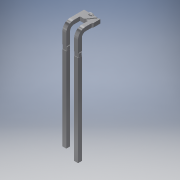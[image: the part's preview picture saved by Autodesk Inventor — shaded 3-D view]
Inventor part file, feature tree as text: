
AUTODESK INVENTOR PART (.ipt)
format: ipt  version: 2019.4 (Build 234330000, 330)  size: 351,744 bytes
history: native  units: mm
features: sketch x8, fillet x4, other x3, revolve x3, extrude x2, projected_geometry x2, sweep x1
ambient origin geometry x8: Origin, YZ Plane, XZ Plane, XY Plane, X Axis, Y Axis, Z Axis, Center Point
bodies: Body1 (feature_tree), Body2 (feature_tree)
feature tree (23):
  other  "Sólido1"
  extrude  "Extrusión1"  Depth=0.98mm
  extrude  "Extrusión2"  Depth=0.98mm
  fillet  "Empalme6"  Radius=4.0mm
  fillet  "Empalme7"  Radius=2.0mm
  fillet  "Empalme8"  Radius=1.0mm
  fillet  "Empalme9"  Radius=4.0mm
  revolve  "Revolución1"  [1 undecoded]
  revolve  "Revolución2"  [1 undecoded]
  revolve  "Revolución3"  [1 undecoded]
  sweep  "Barrido1"
  other  "Bend Part1"
  sketch  "Boceto1"  dims[d0=0.98mm d1=0.98mm]
  sketch  "Boceto2"  dims[d2=4.0mm d3=0.98mm d4=4.0mm d5=2.0mm d6=1.0mm d7=4.0mm]
  sketch  "Boceto3"  dims[d8=2.0mm d9=21.816616mm]
  sketch  "Boceto4"  dims[d10=9.599311mm d11=1.0mm]
  sketch  "Boceto5"  dims[d12=28.1mm d13=1.7mm]
  other  "Sólido2"
  sketch  "Boceto6"  dims[d14=0.98mm d15=0.0mm d16=1.18mm]
  projected_geometry  "Contorno proyectado1"
  projected_geometry  "Contorno proyectado2"
  sketch  "Boceto7"  dims[d17=1.18mm]
  sketch  "Sketch8"  dims[d20=0.1mm d21=0.1mm d22=0.78mm d23=0.0mm d29=0.1mm d30=0.1mm d31=0.1mm d32=0.1mm d33=180.0deg d34=180.0deg d35=180.0deg d36=0.1mm d37=0.0mm d38=0.0mm d40=1.0mm d41=90.0deg d46=3.5mm]
note: 3 required parameter values undecoded (feature->parameter linkage not recoverable at this tier; creation-order binding heuristic only, values carry confidence <= 0.55)
